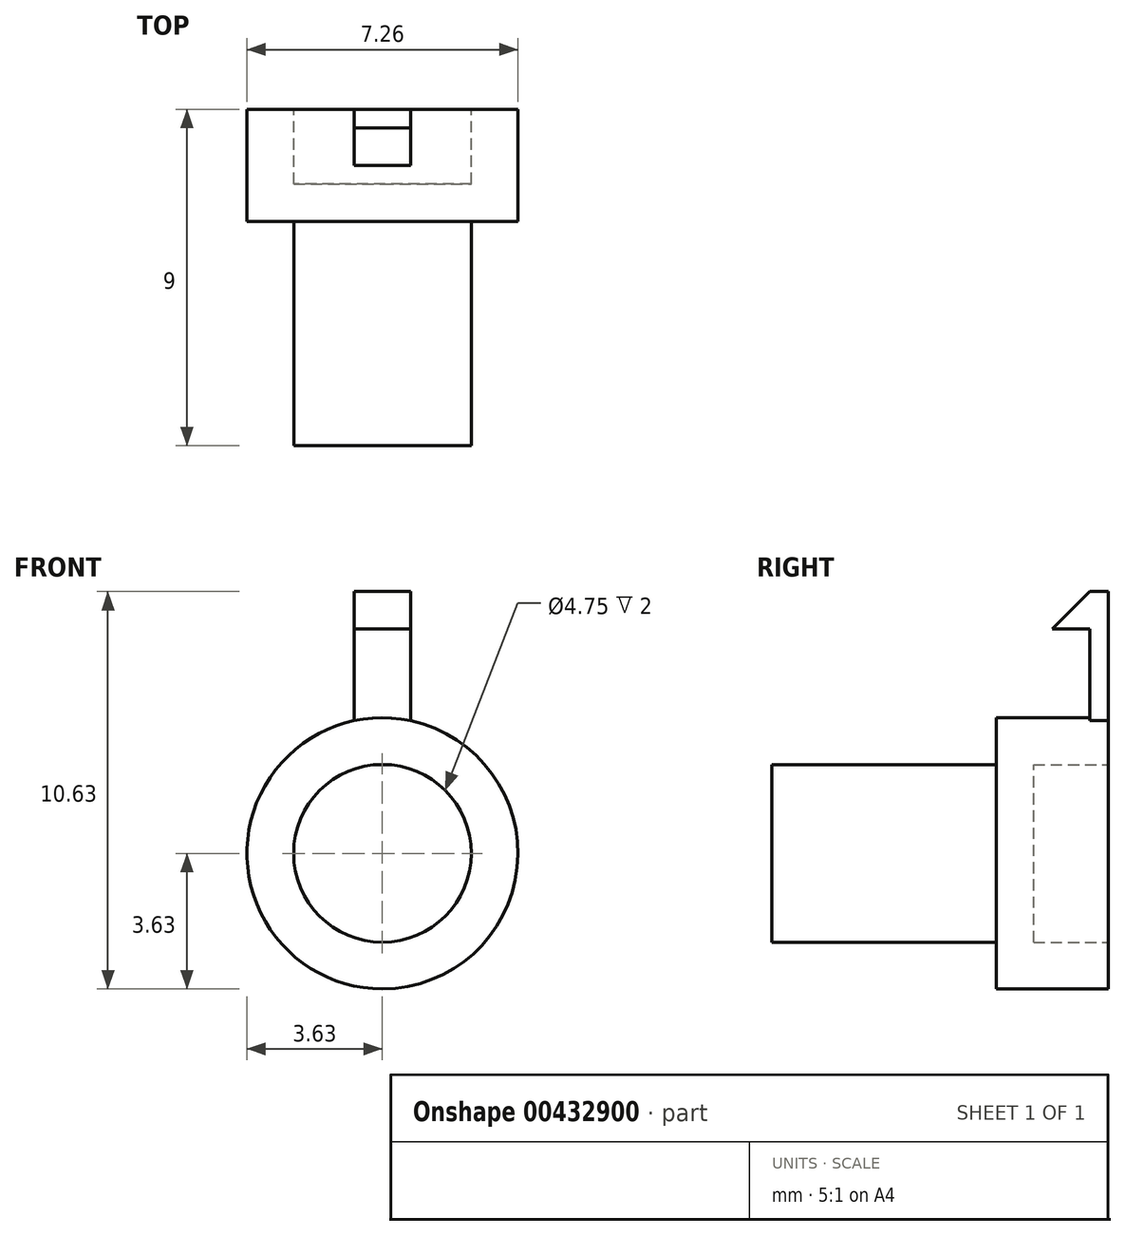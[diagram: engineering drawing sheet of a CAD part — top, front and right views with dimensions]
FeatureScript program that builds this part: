
annotation { "Feature Type Name" : "Feature", "Feature Type Description" : "" }
export const myFeature = defineFeature(function(context is Context, id is Id, definition is map)
    precondition{}
    {
        {
            var Q0;
            Q0=qCreatedBy(makeId("Front.planeOp"),FACE);
            var sketch = newSketch(context, id + "F0", { "sketchPlane" : qUnion([Q0])});
            skCircle(sketch, "E0", {"center": v(0, 0) * mm, "radius": 3.62 * mm});
            skCircle(sketch, "E1", {"center": v(0, 0) * mm, "radius": 2.38 * mm});
            skSolve(sketch);
        }
        {
            var Q0;
            Q0=makeQuery(id+"F0.imprint","IMPRINT",FACE,{"disambiguationData":[TD([[makeQuery(id+"F0.imprint","IMPRINT",EDGE,{"derivedFrom":sQuery(id+"F0.wireOp",EDGE,"E0")}),1.0]])]});
            extrude(context, id + "F1", {"entities" : qUnion([Q0]), "depth" : 1 * mm, "hasSecondDirection" : true, "secondDirectionOppositeDirection" : true, "secondDirectionDepth" : 2 * mm});
        }
        {
            var Q0;
            Q0=makeQuery(id+"F0.imprint","IMPRINT",FACE,{"disambiguationData":[TD([[makeQuery(id+"F0.imprint","IMPRINT",EDGE,{"derivedFrom":sQuery(id+"F0.wireOp",EDGE,"E1")}),1.0]])]});
            extrude(context, id + "F2", {"entities" : qUnion([Q0]), "operationType" : NewBodyOperationType.ADD, "depth" : 7 * mm});
        }
        {
            var Q0;
            Q0=qCreatedBy(makeId("Right.planeOp"),FACE);
            var sketch = newSketch(context, id + "F3", { "sketchPlane" : qUnion([Q0])});
            skLineSegment(sketch, "E2.bottom", {"start": v(2, 3.5) * mm, "end": v(1.5, 3.5) * mm});
            skLineSegment(sketch, "E2.top", {"start": v(2, 7) * mm, "end": v(1.5, 7) * mm});
            skLineSegment(sketch, "E2.left", {"start": v(2, 3.5) * mm, "end": v(2, 7) * mm});
            skLineSegment(sketch, "E2.right", {"start": v(1.5, 3.5) * mm, "end": v(1.5, 7) * mm});
            skLineSegment(sketch, "E3", {"start": v(1.5, 7) * mm, "end": v(0.5, 6) * mm});
            skLineSegment(sketch, "E4", {"start": v(0.5, 6) * mm, "end": v(1.5, 6) * mm});
            skSolve(sketch);
        }
        {
            var Q0;
            {var subQ1=sQuery(id+"F3.wireOp",EDGE,"E2.bottom");Q0=makeQuery(id+"F3.imprint","IMPRINT",FACE,{"disambiguationData":[TD([[makeQuery(id+"F3.imprint","IMPRINT",EDGE,{"derivedFrom":subQ1}),-1.0]])]});}
            var Q1;
            {var subQ0=sQuery(id+"F3.wireOp",EDGE,"E3");Q1=makeQuery(id+"F3.imprint","IMPRINT",FACE,{"disambiguationData":[TD([[makeQuery(id+"F3.imprint","IMPRINT",EDGE,{"derivedFrom":subQ0}),1.0]])]});}
            extrude(context, id + "F4", {"entities" : qUnion([Q0, Q1]), "operationType" : NewBodyOperationType.ADD, "endBound" : BoundingType.SYMMETRIC, "depth" : 1.5 * mm});
        }
    });
